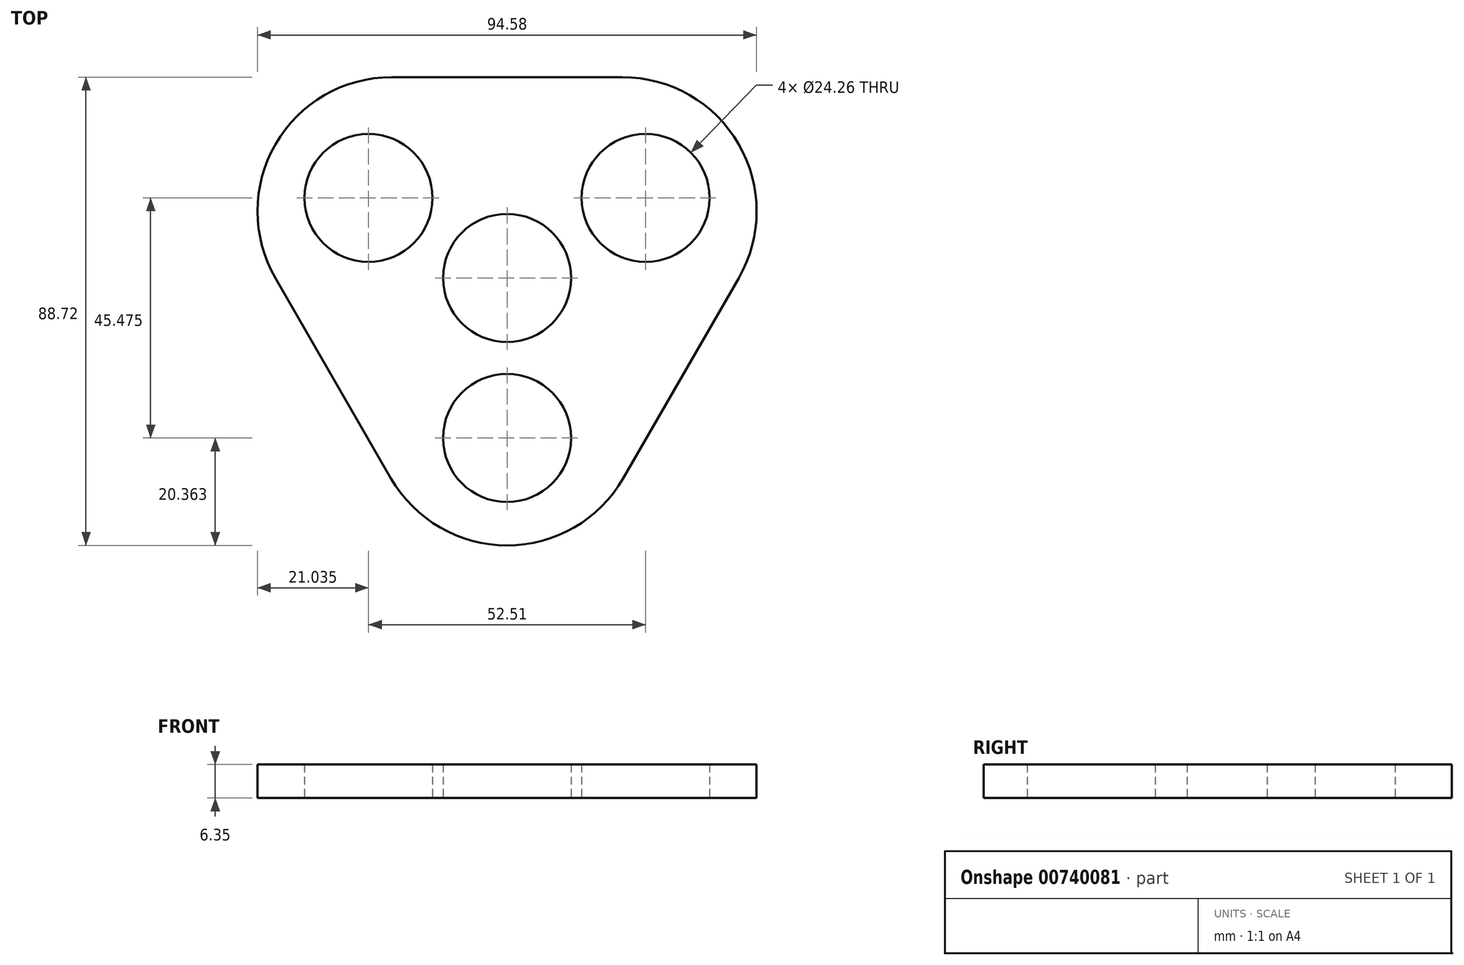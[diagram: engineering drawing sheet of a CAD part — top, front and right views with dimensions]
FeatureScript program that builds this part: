
annotation { "Feature Type Name" : "Feature", "Feature Type Description" : "" }
export const myFeature = defineFeature(function(context is Context, id is Id, definition is map)
    precondition{}
    {
        {
            var Q0;
            Q0=qCreatedBy(makeId("Top.planeOp"),FACE);
            var sketch = newSketch(context, id + "F0", { "sketchPlane" : qUnion([Q0])});
            skCircle(sketch, "E0", {"center": v(0, -0.41) * mm, "radius": 12.13 * mm});
            skCircle(sketch, "E1.cCircle", {"center": v(0, -0.41) * mm, "radius": 38.04 * mm, "construction": true});
            skLineSegment(sketch, "E1.0", {"start": v(65.88, 37.63) * mm, "end": v(0, -76.49) * mm});
            skLineSegment(sketch, "E1.1", {"start": v(0, -76.49) * mm, "end": v(-65.88, 37.63) * mm});
            skLineSegment(sketch, "E1.2", {"start": v(-65.88, 37.63) * mm, "end": v(65.88, 37.63) * mm});
            skPoint(sketch, "E1.0.midPoint", {"position": v(32.94, -19.43) * mm});
            skCircle(sketch, "E2", {"center": v(0, -30.73) * mm, "radius": 12.13 * mm});
            skCircle(sketch, "E3", {"center": v(26.25, 14.75) * mm, "radius": 12.13 * mm});
            skCircle(sketch, "E4", {"center": v(-26.25, 14.75) * mm, "radius": 12.13 * mm});
            skSolve(sketch);
        }
        {
            var Q0;
            Q0 = qSketchRegion(id + "F0", true);
            extrude(context, id + "F1", {"entities" : qUnion([Q0]), "depth" : 6.35 * mm, "offsetDistance" : 25 * mm});
        }
        {
            var Q0;
            Q0=makeQuery(id+"F1.opExtrude","SWEPT_EDGE",EDGE,{"disambiguationData":[OSD([sQuery(id+"F0.wireOp",EDGE,"E1.1"),sQuery(id+"F0.wireOp",EDGE,"E1.2")])]});
            fillet(context, id + "F2", {"entities" : qUnion([Q0]), "radius" : 25.4 * mm, "tangentPropagation" : true, "allowEdgeOverflow" : false});
        }
        {
            var Q0;
            Q0=makeQuery(id+"F1.opExtrude","SWEPT_EDGE",EDGE,{"disambiguationData":[OSD([sQuery(id+"F0.wireOp",EDGE,"E1.0"),sQuery(id+"F0.wireOp",EDGE,"E1.2")])]});
            fillet(context, id + "F3", {"entities" : qUnion([Q0]), "radius" : 25.4 * mm, "tangentPropagation" : true, "allowEdgeOverflow" : false});
        }
        {
            var Q0;
            Q0=makeQuery(id+"F1.opExtrude","SWEPT_EDGE",EDGE,{"disambiguationData":[OSD([sQuery(id+"F0.wireOp",EDGE,"E1.0"),sQuery(id+"F0.wireOp",EDGE,"E1.1")])]});
            fillet(context, id + "F4", {"entities" : qUnion([Q0]), "radius" : 25.4 * mm, "tangentPropagation" : true, "allowEdgeOverflow" : false});
        }
    });
